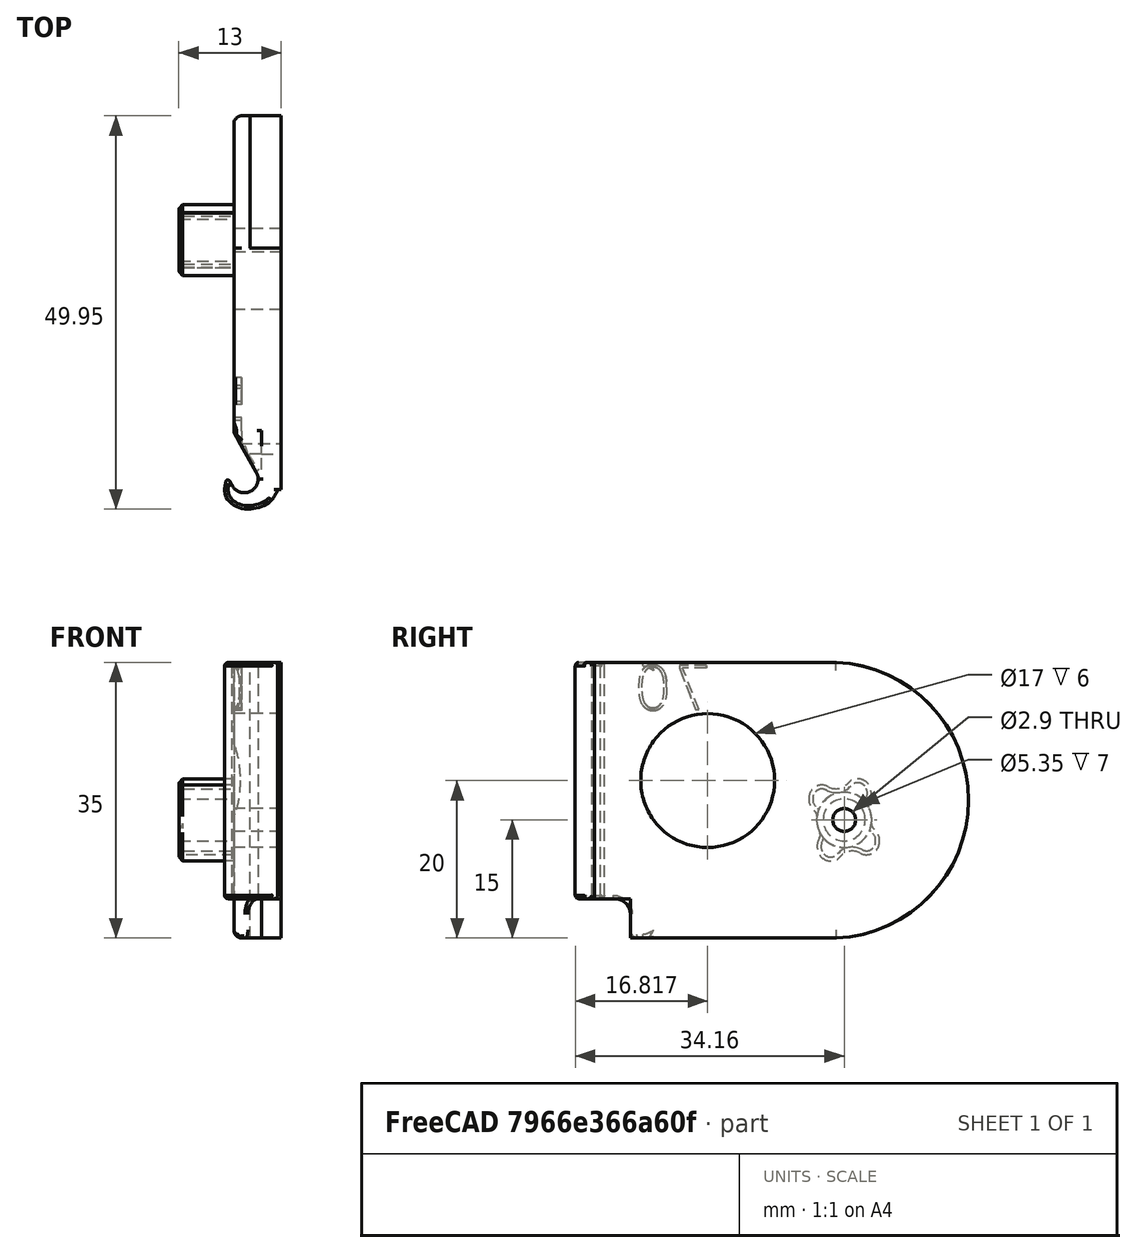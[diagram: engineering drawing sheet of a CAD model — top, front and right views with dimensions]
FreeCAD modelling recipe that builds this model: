
FCSTD DOCUMENT  (FreeCAD 0.18R)
Label: hinge-left-170deg-flat
License: All rights reserved
LicenseURL: http://en.wikipedia.org/wiki/All_rights_reserved
objects: App::FeaturePython×4, Part::FeaturePython×2, Part::Part2DObjectPython×1, Part::Extrusion×1, Part::Cut×1
note: 5 computed .brp shape members not serialized (recipe doc carries the construction recipe); baked Part::Feature solids carry a one-line shape summary decoded from their .brp

FEATURE [Part::FeaturePython] pillar_base_001  label="pillar-base_001"  # a2plus imported part (geometry in sourceFile) (typed FeaturePython)
  Placement = pos=(0.000608724,-2.95131,7.59766) rot=(-1,0,0;0.261974rad)
  a2p_Version = V0.1
  fixedPosition = false
  objectType = a2pPart
  sourceFile = ./parts/pillar-base.fcstd
  subassemblyImport = false
  timeLastImport = 1.60452e+09
  updateColors = true
FEATURE [Part::Part2DObjectPython] ShapeString  # Draft 2D object (typed FeaturePython)
  FontFile = <path>
  Placement = pos=(1.61,10.5,29) rot=(0.57735,-0.57735,-0.57735;2.0944rad)
  Size = 6
  String = 70
  Tracking = 0
FEATURE [Part::Extrusion] Extrude
  Base = -> ShapeString
  Dir = (-1,0,0)
  DirMode = 2
  FaceMakerClass = Part::FaceMakerBullseye
  LengthFwd = 2
  LengthRev = 0
  Solid = false
  Symmetric = false
FEATURE [Part::FeaturePython] bracket_left_flat_001  label="bracket-left-flat_001"  # a2plus imported part (geometry in sourceFile) (typed FeaturePython)
  a2p_Version = V0.1
  fixedPosition = true
  objectType = a2pPart
  sourceFile = ./parts/bracket-left-flat.fcstd
  subassemblyImport = false
  timeLastImport = 1.60454e+09
  updateColors = true
FEATURE [App::FeaturePython] axisCoincident_001  label="axisCoincident_001__bracket-left-flat_001"  # a2plus constraint (typed FeaturePython)
  Object1 = pillar_base_001
  Object2 = bracket_left_flat_001
  ParentTreeObject = -> pillar_base_001
  SubElement1 = Face17
  SubElement2 = Face48
  Suppressed = false
  Type = axial
  directionConstraint = 1
  lockRotation = false
FEATURE [App::FeaturePython] axisCoincident_001_mirror  label="axisCoincident_001__pillar-base_001"  # a2plus constraint (typed FeaturePython)
  Object1 = pillar_base_001
  Object2 = bracket_left_flat_001
  ParentTreeObject = -> bracket_left_flat_001
  SubElement1 = Face17
  SubElement2 = Face48
  Suppressed = false
  Type = axial
  directionConstraint = 1
  lockRotation = false
FEATURE [App::FeaturePython] planeCoincident_001  label="planeCoincident_001__bracket-left-flat_001"  # a2plus constraint (typed FeaturePython)
  Object1 = pillar_base_001
  Object2 = bracket_left_flat_001
  ParentTreeObject = -> pillar_base_001
  SubElement1 = Face1
  SubElement2 = Face72
  Suppressed = false
  Type = plane
  directionConstraint = 0
  offset = 0
FEATURE [App::FeaturePython] planeCoincident_001_mirror  label="planeCoincident_001__pillar-base_001"  # a2plus constraint (typed FeaturePython)
  Object1 = pillar_base_001
  Object2 = bracket_left_flat_001
  ParentTreeObject = -> bracket_left_flat_001
  SubElement1 = Face1
  SubElement2 = Face72
  Suppressed = false
  Type = plane
  directionConstraint = 0
  offset = 0
FEATURE [Part::Cut] Cut
  Base = -> bracket_left_flat_001
  Tool = -> Extrude
note: 1 file-system path scrubbed to <path> (originals preserved in the JSON sidecar)
